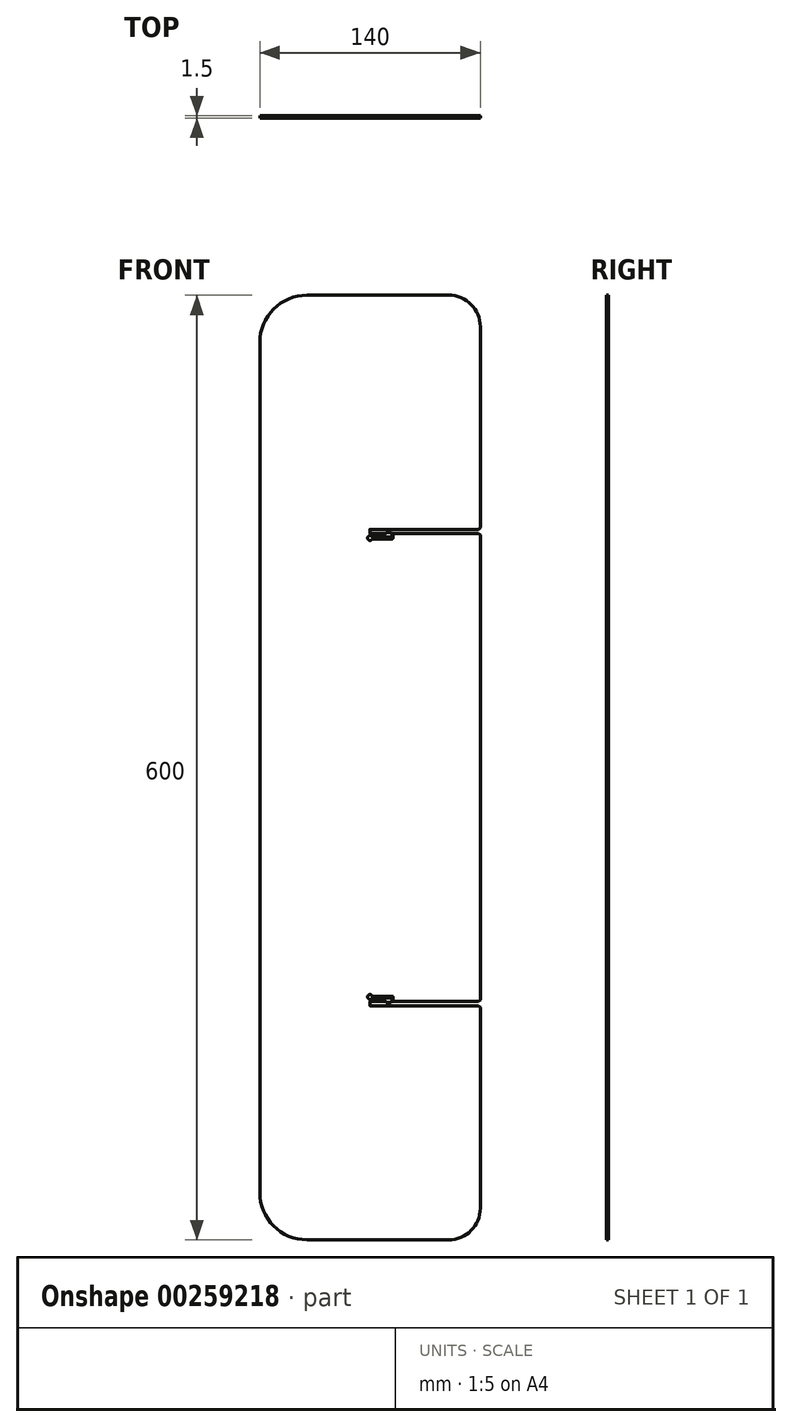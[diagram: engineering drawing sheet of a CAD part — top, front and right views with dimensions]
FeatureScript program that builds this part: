
annotation { "Feature Type Name" : "Feature", "Feature Type Description" : "" }
export const myFeature = defineFeature(function(context is Context, id is Id, definition is map)
    precondition{}
    {
        {
            var Q0;
            Q0=qCreatedBy(makeId("Front.planeOp"),FACE);
            var sketch = newSketch(context, id + "F0", { "sketchPlane" : qUnion([Q0])});
            skLineSegment(sketch, "E0.0", {"start": v(0.1, 1.27) * mm, "end": v(3, 1.27) * mm});
            skLineSegment(sketch, "E1.0", {"start": v(3.2, 1.47) * mm, "end": v(9.8, 1.47) * mm});
            skArc(sketch, "E2.0.0", {"start": v(1.41, 3.75) * mm, "mid": v(0.87, 3.03) * mm, "end": v(0, 2.75) * mm});
            skLineSegment(sketch, "E2.0.3", {"start": v(3, 1.27) * mm, "end": v(3.2, 1.47) * mm});
            skLineSegment(sketch, "E2.0.7", {"start": v(10.13, 0.78) * mm, "end": v(13.05, 0.78) * mm});
            skLineSegment(sketch, "E3.0.6", {"start": v(9.99, 1.33) * mm, "end": v(10.13, 0.78) * mm});
            skArc(sketch, "E3.0.8", {"start": v(13.05, 0.78) * mm, "mid": v(13.13, 0.8) * mm, "end": v(13.2, 0.83) * mm});
            skLineSegment(sketch, "E3.0.9", {"start": v(13.2, 0.83) * mm, "end": v(13.94, 1.58) * mm});
            skLineSegment(sketch, "E3.0.11", {"start": v(14, 1.72) * mm, "end": v(14, 3.55) * mm});
            skLineSegment(sketch, "E3.0.13", {"start": v(13.8, 3.75) * mm, "end": v(1.41, 3.75) * mm});
            skArc(sketch, "E4.0.5", {"start": v(9.8, 1.47) * mm, "mid": v(9.91, 1.43) * mm, "end": v(9.99, 1.33) * mm});
            skArc(sketch, "E4.0.10", {"start": v(13.94, 1.58) * mm, "mid": v(13.98, 1.65) * mm, "end": v(14, 1.72) * mm});
            skArc(sketch, "E5.0.6", {"start": v(14.5, 1.47) * mm, "mid": v(14.56, 1.33) * mm, "end": v(14.7, 1.28) * mm});
            skLineSegment(sketch, "E5.0.13", {"start": v(70, -130) * mm, "end": v(70, -2.27) * mm});
            skLineSegment(sketch, "E6.0.0", {"start": v(0, 0) * mm, "end": v(0, 1.17) * mm});
            skLineSegment(sketch, "E6.0.7", {"start": v(14.7, 1.28) * mm, "end": v(69, 1.28) * mm});
            skLineSegment(sketch, "E6.0.16", {"start": v(0, -1.18) * mm, "end": v(0, 0) * mm});
            skArc(sketch, "E7.0.2", {"start": v(0, 2.75) * mm, "mid": v(-1.22, 5.12) * mm, "end": v(1.41, 4.75) * mm});
            skLineSegment(sketch, "E7.0.3", {"start": v(1.41, 4.75) * mm, "end": v(14.3, 4.75) * mm});
            skLineSegment(sketch, "E7.0.5", {"start": v(14.5, 4.55) * mm, "end": v(14.5, 1.47) * mm});
            skLineSegment(sketch, "E8", {"start": v(-4.63, 0) * mm, "end": v(42.86, 0) * mm, "construction": true});
            skPoint(sketch, "E9", {"position": v(10, 1.28) * mm});
            skLineSegment(sketch, "E10", {"start": v(-70, -120) * mm, "end": v(-70, 420) * mm});
            skLineSegment(sketch, "E11", {"start": v(-47.13, 150) * mm, "end": v(117.4, 150) * mm, "construction": true});
            skLineSegment(sketch, "E12", {"start": v(-40, -150) * mm, "end": v(50, -150) * mm});
            skLineSegment(sketch, "E13.MirrorCS", {"start": v(-40, 450) * mm, "end": v(50, 450) * mm});
            skLineSegment(sketch, "E14.trimOffspring", {"start": v(70, 150) * mm, "end": v(70, 2.27) * mm});
            skPoint(sketch, "E15.visualSharp", {"position": v(-70, 450) * mm});
            skArc(sketch, "E15.filletArc", {"start": v(-40, 450) * mm, "mid": v(-61.21, 441.21) * mm, "end": v(-70, 420) * mm});
            skPoint(sketch, "E16.visualSharp", {"position": v(-70, -150) * mm});
            skArc(sketch, "E16.filletArc", {"start": v(-70, -120) * mm, "mid": v(-61.21, -141.21) * mm, "end": v(-40, -150) * mm});
            skPoint(sketch, "E17.visualSharp", {"position": v(70, -150) * mm});
            skArc(sketch, "E17.filletArc", {"start": v(50, -150) * mm, "mid": v(64.14, -144.14) * mm, "end": v(70, -130) * mm});
            skPoint(sketch, "E18.visualSharp", {"position": v(70, 450) * mm});
            skArc(sketch, "E18.filletArc", {"start": v(70, 430) * mm, "mid": v(64.14, 444.14) * mm, "end": v(50, 450) * mm});
            skArc(sketch, "E19", {"start": v(0.1, 1.27) * mm, "mid": v(-0.07, 1.35) * mm, "end": v(0, 1.17) * mm});
            skArc(sketch, "E20", {"start": v(0, -1.18) * mm, "mid": v(-0.07, -1.35) * mm, "end": v(0.1, -1.28) * mm});
            skPoint(sketch, "E21.orphan", {"position": v(0, 0.75) * mm});
            skLineSegment(sketch, "E22", {"start": v(0, 150) * mm, "end": v(0, -170.54) * mm, "construction": true});
            skPoint(sketch, "E23", {"position": v(0, 0) * mm});
            skCircle(sketch, "E24", {"center": v(0, 0) * mm, "radius": 1.27 * mm, "construction": true});
            skPoint(sketch, "E25.newPointA", {"position": v(14.3, 4.75) * mm});
            skArc(sketch, "E25.filletArc", {"start": v(14.5, 4.55) * mm, "mid": v(14.44, 4.7) * mm, "end": v(14.3, 4.75) * mm});
            skPoint(sketch, "E26.newPointA", {"position": v(13.8, 3.75) * mm});
            skArc(sketch, "E26.filletArc", {"start": v(14, 3.55) * mm, "mid": v(13.94, 3.7) * mm, "end": v(13.8, 3.75) * mm});
            skArc(sketch, "E27.MirrorCS", {"start": v(0.1, 298.73) * mm, "mid": v(-0.07, 298.65) * mm, "end": v(0, 298.82) * mm});
            skArc(sketch, "E28.MirrorCS", {"start": v(0, 301.18) * mm, "mid": v(-0.07, 301.35) * mm, "end": v(0.1, 301.28) * mm});
            skCircle(sketch, "E29.MirrorC", {"center": v(0, 300) * mm, "radius": 1.27 * mm, "construction": true});
            skArc(sketch, "E30.MirrorCS", {"start": v(14, 296.45) * mm, "mid": v(13.94, 296.3) * mm, "end": v(13.8, 296.25) * mm});
            skLineSegment(sketch, "E31.MirrorCS", {"start": v(0, 300) * mm, "end": v(0, 298.82) * mm});
            skLineSegment(sketch, "E32.MirrorCS", {"start": v(0, 301.17) * mm, "end": v(0, 300) * mm});
            skArc(sketch, "E33.MirrorCS", {"start": v(14.5, 295.45) * mm, "mid": v(14.44, 295.3) * mm, "end": v(14.3, 295.25) * mm});
            skLineSegment(sketch, "E34.MirrorCS", {"start": v(14.5, 295.45) * mm, "end": v(14.5, 298.52) * mm});
            skLineSegment(sketch, "E35.MirrorCS", {"start": v(14, 298.28) * mm, "end": v(14, 296.45) * mm});
            skArc(sketch, "E36.MirrorCS", {"start": v(9.8, 298.52) * mm, "mid": v(9.91, 298.57) * mm, "end": v(9.99, 298.67) * mm});
            skLineSegment(sketch, "E37.MirrorCS", {"start": v(9.99, 298.67) * mm, "end": v(10.13, 299.22) * mm});
            skLineSegment(sketch, "E38.MirrorCS", {"start": v(0.1, 298.73) * mm, "end": v(3, 298.73) * mm});
            skLineSegment(sketch, "E39.MirrorCS", {"start": v(10.13, 299.22) * mm, "end": v(13.05, 299.22) * mm});
            skArc(sketch, "E40.MirrorCS", {"start": v(14.5, 298.52) * mm, "mid": v(14.56, 298.67) * mm, "end": v(14.7, 298.72) * mm});
            skLineSegment(sketch, "E41.MirrorCS", {"start": v(13.2, 299.17) * mm, "end": v(13.94, 298.42) * mm});
            skLineSegment(sketch, "E42.MirrorCS", {"start": v(3, 298.72) * mm, "end": v(3.2, 298.52) * mm});
            skArc(sketch, "E43.MirrorCS", {"start": v(13.05, 299.22) * mm, "mid": v(13.13, 299.2) * mm, "end": v(13.2, 299.17) * mm});
            skArc(sketch, "E44.MirrorCS", {"start": v(13.94, 298.42) * mm, "mid": v(13.98, 298.35) * mm, "end": v(14, 298.28) * mm});
            skArc(sketch, "E45.MirrorCS", {"start": v(1.41, 296.25) * mm, "mid": v(0.87, 296.97) * mm, "end": v(0, 297.25) * mm});
            skLineSegment(sketch, "E46.MirrorCS", {"start": v(3.2, 298.52) * mm, "end": v(9.8, 298.52) * mm});
            skPoint(sketch, "E47.MirrorP", {"position": v(0, 299.25) * mm});
            skPoint(sketch, "E48.MirrorP", {"position": v(14.3, 295.25) * mm});
            skLineSegment(sketch, "E49.MirrorCS", {"start": v(-4.63, 300) * mm, "end": v(42.86, 300) * mm, "construction": true});
            skArc(sketch, "E50.MirrorCS", {"start": v(0, 297.25) * mm, "mid": v(-1.22, 294.88) * mm, "end": v(1.41, 295.25) * mm});
            skPoint(sketch, "E51.MirrorP", {"position": v(10, 298.72) * mm});
            skPoint(sketch, "E52.MirrorP", {"position": v(13.8, 296.25) * mm});
            skLineSegment(sketch, "E53.MirrorCS", {"start": v(13.8, 296.25) * mm, "end": v(1.41, 296.25) * mm});
            skLineSegment(sketch, "E54.MirrorCS", {"start": v(1.41, 295.25) * mm, "end": v(14.3, 295.25) * mm});
            skPoint(sketch, "E55.orphan", {"position": v(0, 6.6) * mm});
            skPoint(sketch, "E56.orphan", {"position": v(0, -2.3) * mm});
            skLineSegment(sketch, "E57.MirrorCS", {"start": v(0, 150) * mm, "end": v(0, 470.54) * mm, "construction": true});
            skLineSegment(sketch, "E58", {"start": v(70, 2.27) * mm, "end": v(69, 1.28) * mm});
            skLineSegment(sketch, "E59", {"start": v(14.7, -1.28) * mm, "end": v(0, -1.28) * mm});
            skLineSegment(sketch, "E60.MirrorCS", {"start": v(14.7, -1.28) * mm, "end": v(69, -1.27) * mm});
            skLineSegment(sketch, "E61.MirrorCS", {"start": v(70, -2.27) * mm, "end": v(69, -1.27) * mm});
            skLineSegment(sketch, "E62.MirrorCS", {"start": v(70, -297.73) * mm, "end": v(39, -298.73) * mm});
            skLineSegment(sketch, "E63.MirrorCS", {"start": v(14.7, 301.28) * mm, "end": v(0, 301.28) * mm});
            skLineSegment(sketch, "E64.MirrorCS", {"start": v(14.7, 301.28) * mm, "end": v(69, 301.27) * mm});
            skLineSegment(sketch, "E65.MirrorCS", {"start": v(70, 302.27) * mm, "end": v(69, 301.27) * mm});
            skLineSegment(sketch, "E66.MirrorCS", {"start": v(70, 430) * mm, "end": v(70, 302.27) * mm});
            skLineSegment(sketch, "E67.MirrorCS", {"start": v(14.7, 298.72) * mm, "end": v(69, 298.72) * mm});
            skLineSegment(sketch, "E68.MirrorCS", {"start": v(70, 297.73) * mm, "end": v(69, 298.73) * mm});
            skLineSegment(sketch, "E69.MirrorCS", {"start": v(70, 150) * mm, "end": v(70, 297.73) * mm});
            skSolve(sketch);
        }
        {
            var Q0;
            Q0=qSketchRegion(id+"F0",true);
            extrude(context, id + "F1", {"entities" : qUnion([Q0]), "depth" : 0.75 * mm, "hasSecondDirection" : true, "secondDirectionOppositeDirection" : true, "secondDirectionDepth" : 0.75 * mm});
        }
    });
